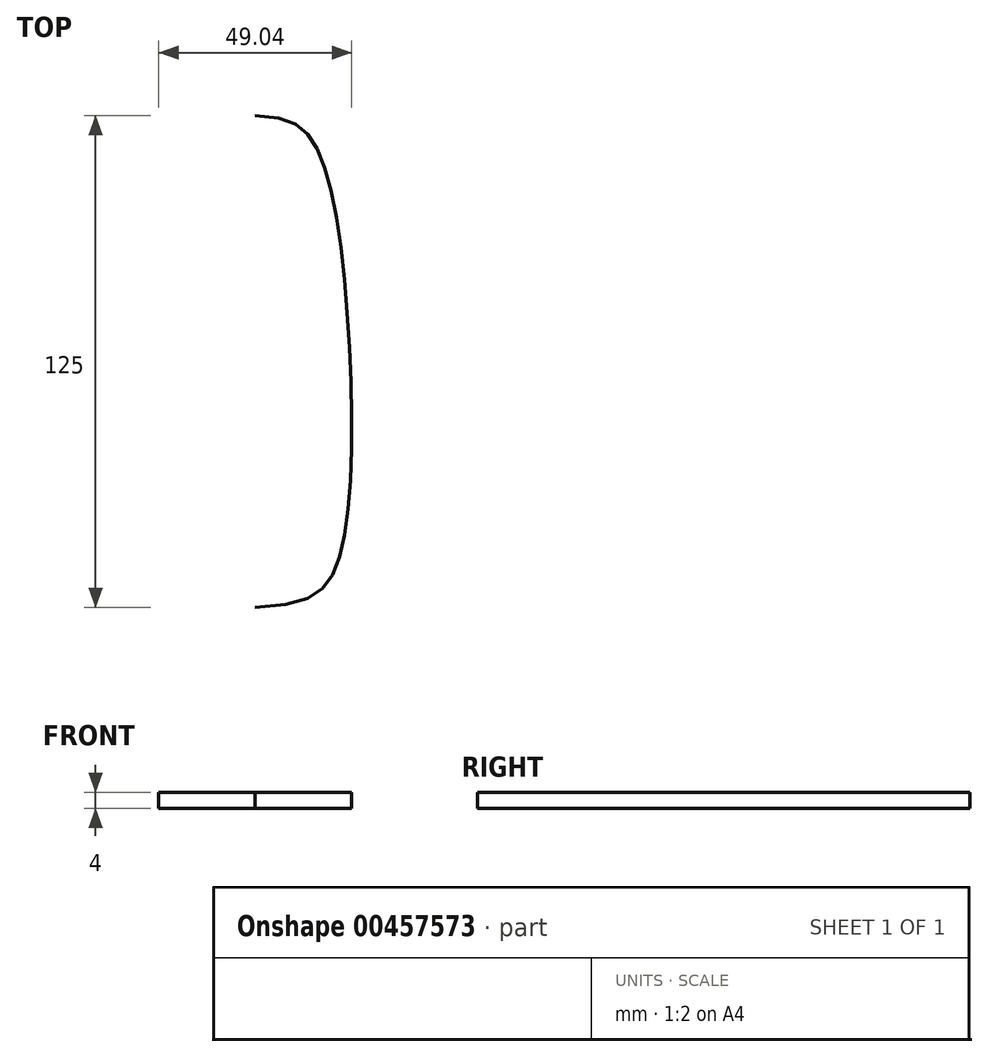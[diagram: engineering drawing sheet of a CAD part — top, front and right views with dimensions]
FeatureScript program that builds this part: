
annotation { "Feature Type Name" : "Feature", "Feature Type Description" : "" }
export const myFeature = defineFeature(function(context is Context, id is Id, definition is map)
    precondition{}
    {
        {
            var Q0;
            Q0=qCreatedBy(makeId("Top.planeOp"),FACE);
            var sketch = newSketch(context, id + "F0", { "sketchPlane" : qUnion([Q0])});
            skFitSpline(sketch, "E0", {"points": [v(0, 60.44) * mm, v(-16, 51.38) * mm, v(-24, 0) * mm, v(-21, -52.87) * mm, v(0, -64.56) * mm], "startDerivative": vector(-157.32, -6.84) * mm, "endDerivative": vector(207.05, -9.13) * mm});
            skFitSpline(sketch, "E1.MirrorCS", {"points": [v(0, 60.44) * mm, v(16, 51.38) * mm, v(24, 0) * mm, v(21, -52.87) * mm, v(0, -64.56) * mm], "startDerivative": vector(157.32, -6.84) * mm, "endDerivative": vector(-207.05, -9.13) * mm});
            skSolve(sketch);
        }
        {
            var Q0;
            Q0=makeQuery(id+"F0.imprint","IMPRINT",FACE,{"disambiguationData":[TD([[makeQuery(id+"F0.imprint","IMPRINT",EDGE,{"derivedFrom":sQuery(id+"F0.wireOp",EDGE,"E0")}),1.0]])]});
            extrude(context, id + "F1", {"entities" : qUnion([Q0]), "depth" : 4 * mm});
        }
    });
